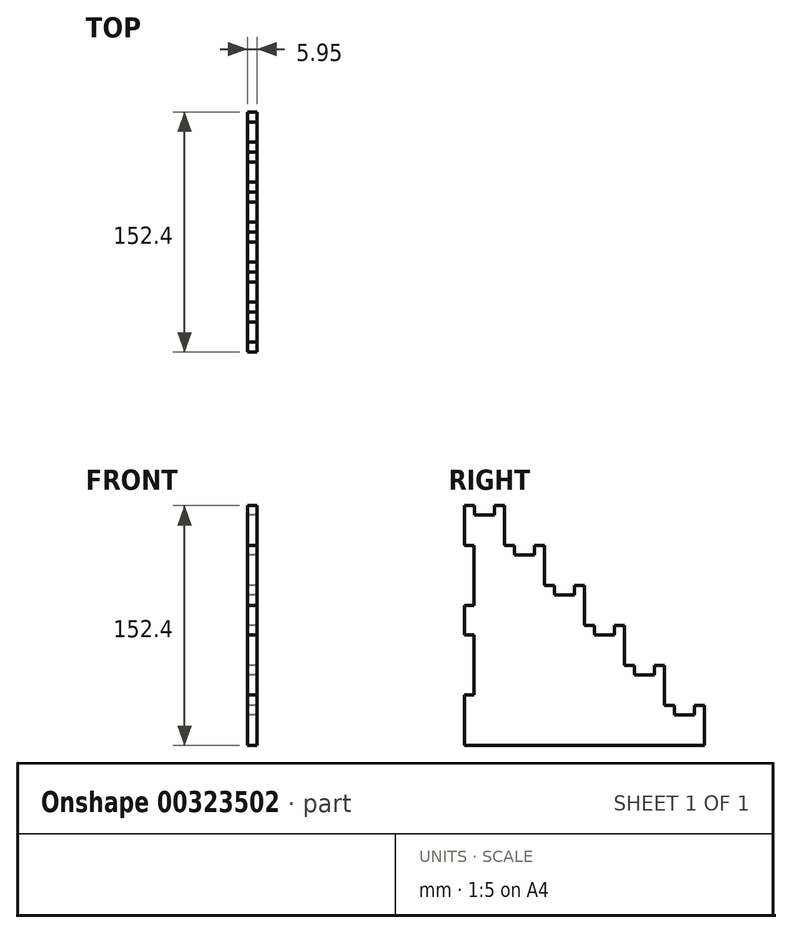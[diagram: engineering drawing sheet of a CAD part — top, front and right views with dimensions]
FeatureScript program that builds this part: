
annotation { "Feature Type Name" : "Feature", "Feature Type Description" : "" }
export const myFeature = defineFeature(function(context is Context, id is Id, definition is map)
    precondition{}
    {
        {
            var Q0;
            Q0=qCreatedBy(makeId("Right.planeOp"),FACE);
            var sketch = newSketch(context, id + "F0", { "sketchPlane" : qUnion([Q0])});
            skLineSegment(sketch, "E0.bottom", {"start": v(-76.2, 72.49) * mm, "end": v(76.2, 72.49) * mm});
            skLineSegment(sketch, "E0.top", {"start": v(-76.2, -79.91) * mm, "end": v(76.2, -79.91) * mm});
            skLineSegment(sketch, "E0.left", {"start": v(-76.2, 72.49) * mm, "end": v(-76.2, -79.91) * mm});
            skLineSegment(sketch, "E0.right", {"start": v(76.2, 72.49) * mm, "end": v(76.2, -79.91) * mm});
            skLineSegment(sketch, "E1.bottom", {"start": v(76.2, 72.49) * mm, "end": v(50.8, 72.49) * mm});
            skLineSegment(sketch, "E1.top", {"start": v(76.2, -54.51) * mm, "end": v(50.8, -54.51) * mm});
            skLineSegment(sketch, "E1.left", {"start": v(76.2, 72.49) * mm, "end": v(76.2, -54.51) * mm});
            skLineSegment(sketch, "E1.right", {"start": v(50.8, 72.49) * mm, "end": v(50.8, -54.51) * mm});
            skLineSegment(sketch, "E2.bottom", {"start": v(50.8, 72.49) * mm, "end": v(25.4, 72.49) * mm});
            skLineSegment(sketch, "E2.top", {"start": v(50.8, -29.11) * mm, "end": v(25.4, -29.11) * mm});
            skLineSegment(sketch, "E2.left", {"start": v(50.8, 72.49) * mm, "end": v(50.8, -29.11) * mm});
            skLineSegment(sketch, "E2.right", {"start": v(25.4, 72.49) * mm, "end": v(25.4, -29.11) * mm});
            skLineSegment(sketch, "E3.bottom", {"start": v(25.4, 72.49) * mm, "end": v(0, 72.49) * mm});
            skLineSegment(sketch, "E3.top", {"start": v(25.4, -3.71) * mm, "end": v(0, -3.71) * mm});
            skLineSegment(sketch, "E3.left", {"start": v(25.4, 72.49) * mm, "end": v(25.4, -3.71) * mm});
            skLineSegment(sketch, "E3.right", {"start": v(0, 72.49) * mm, "end": v(0, -3.71) * mm});
            skLineSegment(sketch, "E4.bottom", {"start": v(0, 72.49) * mm, "end": v(-25.4, 72.49) * mm});
            skLineSegment(sketch, "E4.top", {"start": v(0, 21.69) * mm, "end": v(-25.4, 21.69) * mm});
            skLineSegment(sketch, "E4.left", {"start": v(0, 72.49) * mm, "end": v(0, 21.69) * mm});
            skLineSegment(sketch, "E4.right", {"start": v(-25.4, 72.49) * mm, "end": v(-25.4, 21.69) * mm});
            skLineSegment(sketch, "E5.bottom", {"start": v(-25.4, 72.49) * mm, "end": v(-50.8, 72.49) * mm});
            skLineSegment(sketch, "E5.top", {"start": v(-25.4, 47.09) * mm, "end": v(-50.8, 47.09) * mm});
            skLineSegment(sketch, "E5.left", {"start": v(-25.4, 72.49) * mm, "end": v(-25.4, 47.09) * mm});
            skLineSegment(sketch, "E5.right", {"start": v(-50.8, 72.49) * mm, "end": v(-50.8, 47.09) * mm});
            skLineSegment(sketch, "E6.bottom", {"start": v(-76.2, 47.09) * mm, "end": v(-70.25, 47.09) * mm});
            skLineSegment(sketch, "E6.top", {"start": v(-76.2, 8.99) * mm, "end": v(-70.25, 8.99) * mm});
            skLineSegment(sketch, "E6.left", {"start": v(-76.2, 47.09) * mm, "end": v(-76.2, 8.99) * mm});
            skLineSegment(sketch, "E6.right", {"start": v(-70.25, 47.09) * mm, "end": v(-70.25, 8.99) * mm});
            skLineSegment(sketch, "E7.bottom", {"start": v(-76.2, -47.76) * mm, "end": v(-70.25, -47.76) * mm});
            skLineSegment(sketch, "E7.top", {"start": v(-76.2, -9.66) * mm, "end": v(-70.25, -9.66) * mm});
            skLineSegment(sketch, "E7.left", {"start": v(-76.2, -47.76) * mm, "end": v(-76.2, -9.66) * mm});
            skLineSegment(sketch, "E7.right", {"start": v(-70.25, -47.76) * mm, "end": v(-70.25, -9.66) * mm});
            skLineSegment(sketch, "E8.bottom", {"start": v(57.15, -54.51) * mm, "end": v(69.85, -54.51) * mm});
            skLineSegment(sketch, "E8.top", {"start": v(57.15, -60.46) * mm, "end": v(69.85, -60.46) * mm});
            skLineSegment(sketch, "E8.left", {"start": v(57.15, -54.51) * mm, "end": v(57.15, -60.46) * mm});
            skLineSegment(sketch, "E8.right", {"start": v(69.85, -54.51) * mm, "end": v(69.85, -60.46) * mm});
            skLineSegment(sketch, "E9.bottom", {"start": v(44.45, -29.11) * mm, "end": v(31.75, -29.11) * mm});
            skLineSegment(sketch, "E9.top", {"start": v(44.45, -35.06) * mm, "end": v(31.75, -35.06) * mm});
            skLineSegment(sketch, "E9.left", {"start": v(44.45, -29.11) * mm, "end": v(44.45, -35.06) * mm});
            skLineSegment(sketch, "E9.right", {"start": v(31.75, -29.11) * mm, "end": v(31.75, -35.06) * mm});
            skLineSegment(sketch, "E10.bottom", {"start": v(19.05, -3.71) * mm, "end": v(6.35, -3.71) * mm});
            skLineSegment(sketch, "E10.top", {"start": v(19.05, -9.66) * mm, "end": v(6.35, -9.66) * mm});
            skLineSegment(sketch, "E10.left", {"start": v(19.05, -3.71) * mm, "end": v(19.05, -9.66) * mm});
            skLineSegment(sketch, "E10.right", {"start": v(6.35, -3.71) * mm, "end": v(6.35, -9.66) * mm});
            skLineSegment(sketch, "E11.bottom", {"start": v(-6.35, 21.69) * mm, "end": v(-19.05, 21.69) * mm});
            skLineSegment(sketch, "E11.top", {"start": v(-6.35, 15.74) * mm, "end": v(-19.05, 15.74) * mm});
            skLineSegment(sketch, "E11.left", {"start": v(-6.35, 21.69) * mm, "end": v(-6.35, 15.74) * mm});
            skLineSegment(sketch, "E11.right", {"start": v(-19.05, 21.69) * mm, "end": v(-19.05, 15.74) * mm});
            skLineSegment(sketch, "E12.bottom", {"start": v(-44.45, 47.09) * mm, "end": v(-31.75, 47.09) * mm});
            skLineSegment(sketch, "E12.top", {"start": v(-44.45, 41.14) * mm, "end": v(-31.75, 41.14) * mm});
            skLineSegment(sketch, "E12.left", {"start": v(-44.45, 47.09) * mm, "end": v(-44.45, 41.14) * mm});
            skLineSegment(sketch, "E12.right", {"start": v(-31.75, 47.09) * mm, "end": v(-31.75, 41.14) * mm});
            skLineSegment(sketch, "E13.bottom", {"start": v(-69.85, 72.49) * mm, "end": v(-57.15, 72.49) * mm});
            skLineSegment(sketch, "E13.top", {"start": v(-69.85, 66.54) * mm, "end": v(-57.15, 66.54) * mm});
            skLineSegment(sketch, "E13.left", {"start": v(-69.85, 72.49) * mm, "end": v(-69.85, 66.54) * mm});
            skLineSegment(sketch, "E13.right", {"start": v(-57.15, 72.49) * mm, "end": v(-57.15, 66.54) * mm});
            skSolve(sketch);
        }
        {
            var Q0;
            {var subQ18=sQuery(id+"F0.wireOp",EDGE,"E0.top");Q0=makeQuery(id+"F0.imprint","IMPRINT",FACE,{"disambiguationData":[TD([[makeQuery(id+"F0.imprint","IMPRINT",EDGE,{"derivedFrom":subQ18}),1.0]])]});}
            extrude(context, id + "F1", {"entities" : qUnion([Q0]), "depth" : 5.95 * mm});
        }
    });
